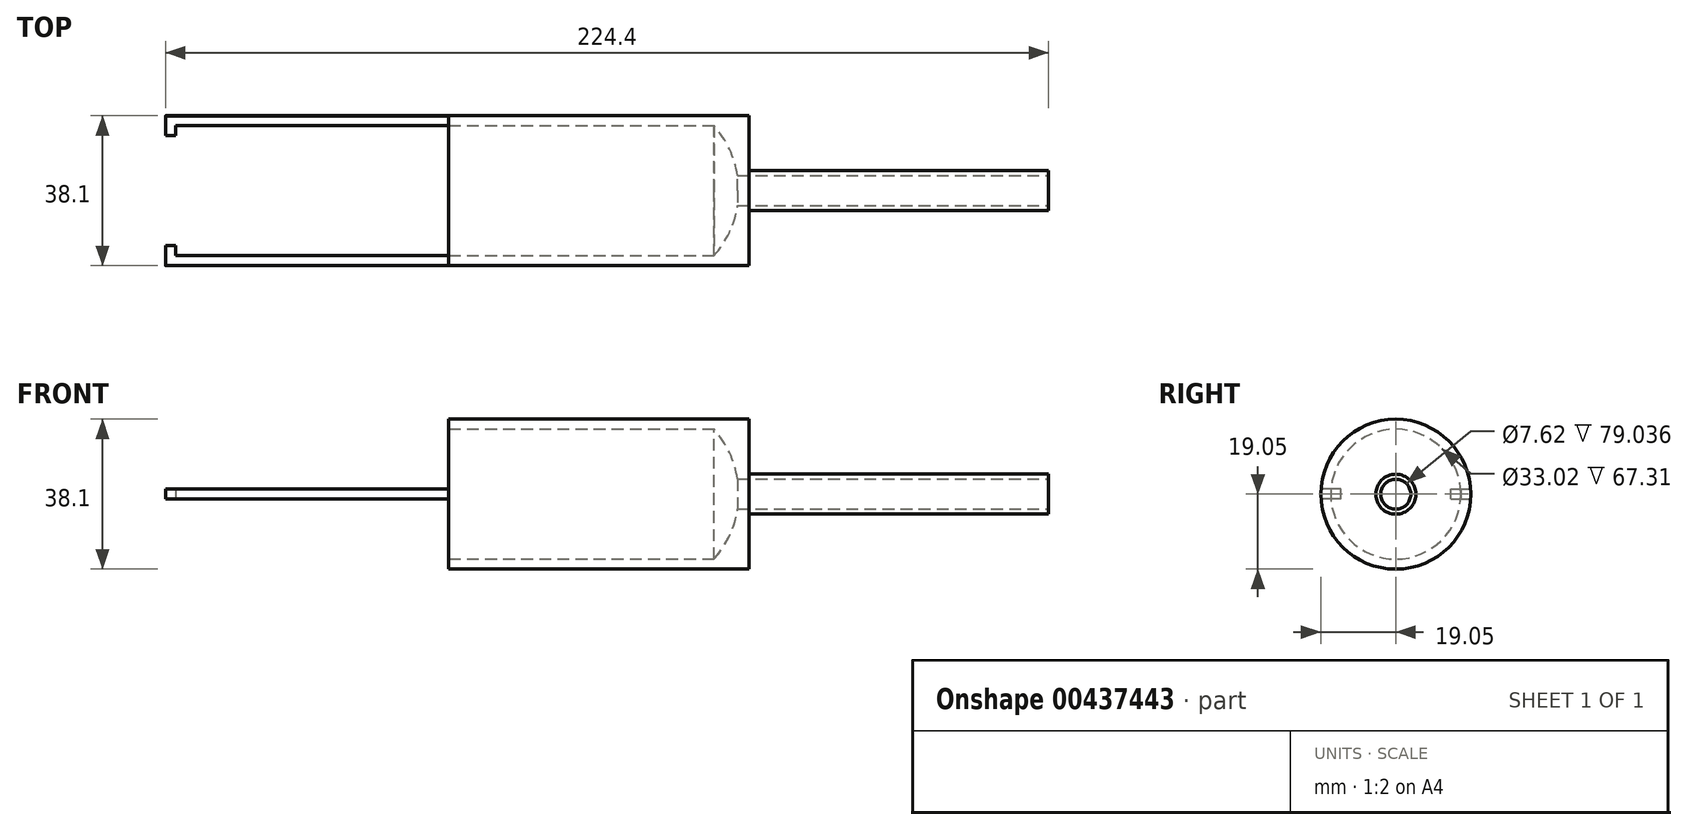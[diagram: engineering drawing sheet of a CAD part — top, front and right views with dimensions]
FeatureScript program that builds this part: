
annotation { "Feature Type Name" : "Feature", "Feature Type Description" : "" }
export const myFeature = defineFeature(function(context is Context, id is Id, definition is map)
    precondition{}
    {
        {
            var Q0;
            Q0=qCreatedBy(makeId("Right.planeOp"),FACE);
            var sketch = newSketch(context, id + "F0", { "sketchPlane" : qUnion([Q0])});
            skCircle(sketch, "E0", {"center": v(0, 0) * mm, "radius": 19.05 * mm});
            skSolve(sketch);
        }
        {
            var Q0;
            Q0=makeQuery(id+"F0.imprint","IMPRINT",FACE,{"disambiguationData":[TD([[makeQuery(id+"F0.imprint","IMPRINT",EDGE,{"derivedFrom":sQuery(id+"F0.wireOp",EDGE,"E0")}),1.0]])]});
            extrude(context, id + "F1", {"entities" : qUnion([Q0]), "depth" : -76.2 * mm});
        }
        {
            var Q0;
            Q0=makeQuery(id+"F1.opExtrude","CAP_FACE",FACE,{"disambiguationData":[OSD([sQuery(id+"F0.wireOp",EDGE,"E0")])],"isStart":true});
            var sketch = newSketch(context, id + "F2", { "sketchPlane" : qUnion([Q0])});
            skCircle(sketch, "E1", {"center": v(0, 0) * mm, "radius": 5.08 * mm});
            skSolve(sketch);
        }
        {
            var Q0;
            Q0=makeQuery(id+"F2.imprint","IMPRINT",FACE,{"disambiguationData":[TD([[makeQuery(id+"F2.imprint","IMPRINT",EDGE,{"derivedFrom":sQuery(id+"F2.wireOp",EDGE,"E1")}),1.0]])]});
            extrude(context, id + "F3", {"entities" : qUnion([Q0]), "operationType" : NewBodyOperationType.ADD, "depth" : 76.2 * mm});
        }
        {
            var Q0;
            Q0=makeQuery(id+"F3.opExtrude","CAP_FACE",FACE,{"disambiguationData":[OSD([sQuery(id+"F2.wireOp",EDGE,"E1")])],"isStart":false});
            var sketch = newSketch(context, id + "F4", { "sketchPlane" : qUnion([Q0])});
            skCircle(sketch, "E2", {"center": v(0, 0) * mm, "radius": 3.81 * mm});
            skSolve(sketch);
        }
        {
            var Q0;
            Q0=makeQuery(id+"F4.imprint","IMPRINT",FACE,{"disambiguationData":[TD([[makeQuery(id+"F4.imprint","IMPRINT",EDGE,{"derivedFrom":sQuery(id+"F4.wireOp",EDGE,"E2")}),1.0]])]});
            extrude(context, id + "F5", {"entities" : qUnion([Q0]), "operationType" : NewBodyOperationType.REMOVE, "oppositeDirection" : true, "depth" : 88.9 * mm});
        }
        {
            var Q0;
            Q0=qCreatedBy(makeId("Front.planeOp"),FACE);
            var sketch = newSketch(context, id + "F6", { "sketchPlane" : qUnion([Q0])});
            skLineSegment(sketch, "E3", {"start": v(-76.2, 0) * mm, "end": v(-2.54, 0) * mm});
            skPoint(sketch, "E4", {"position": v(-8.9, 0) * mm});
            skLineSegment(sketch, "E5", {"start": v(-8.9, -16.51) * mm, "end": v(-8.9, 0) * mm});
            skArc(sketch, "E6", {"start": v(-8.9, -16.51) * mm, "mid": v(-4.18, -8.84) * mm, "end": v(-2.54, 0) * mm});
            skPoint(sketch, "E7.orphan", {"position": v(-8.9, 16.51) * mm});
            skLineSegment(sketch, "E8", {"start": v(-76.2, 0) * mm, "end": v(-76.2, -16.51) * mm});
            skLineSegment(sketch, "E9", {"start": v(-76.2, -16.51) * mm, "end": v(-8.9, -16.51) * mm});
            skSolve(sketch);
        }
        {
            var Q0;
            Q0 = qSketchRegion(id + "F6", true);
            var Q1;
            Q1=sQuery(id+"F6.wireOp",EDGE,"E3");
            revolve(context, id + "F7", {"operationType" : NewBodyOperationType.REMOVE, "entities" : qUnion([Q0]), "axis" : qUnion([Q1]), "revolveType" : RevolveType.FULL, "oppositeDirection" : true});
        }
        {
            var Q0;
            Q0=makeQuery(id+"F1.opExtrude","CAP_FACE",FACE,{"disambiguationData":[OSD([sQuery(id+"F0.wireOp",EDGE,"E0")])],"isStart":false});
            var sketch = newSketch(context, id + "F8", { "sketchPlane" : qUnion([Q0])});
            skLineSegment(sketch, "E10", {"start": v(19.05, 0) * mm, "end": v(-19.05, 0) * mm});
            skPoint(sketch, "E11", {"position": v(-16.51, 0) * mm});
            skPoint(sketch, "E12", {"position": v(16.51, 0) * mm});
            skLineSegment(sketch, "E13", {"start": v(16.51, 0) * mm, "end": v(16.51, 1.27) * mm});
            skLineSegment(sketch, "E14", {"start": v(16.51, 0) * mm, "end": v(16.51, -1.27) * mm});
            skLineSegment(sketch, "E15", {"start": v(16.51, 1.27) * mm, "end": v(13.97, 1.27) * mm});
            skLineSegment(sketch, "E16", {"start": v(16.51, -1.27) * mm, "end": v(13.97, -1.27) * mm});
            skLineSegment(sketch, "E17", {"start": v(13.97, -1.27) * mm, "end": v(13.97, 1.27) * mm});
            skLineSegment(sketch, "E18", {"start": v(0, 0) * mm, "end": v(0, -5.83) * mm});
            skLineSegment(sketch, "E19.MirrorCS", {"start": v(-16.51, 1.27) * mm, "end": v(-13.97, 1.27) * mm});
            skLineSegment(sketch, "E20.MirrorCS", {"start": v(-13.97, -1.27) * mm, "end": v(-13.97, 1.27) * mm});
            skLineSegment(sketch, "E21.MirrorCS", {"start": v(-16.51, -1.27) * mm, "end": v(-13.97, -1.27) * mm});
            skLineSegment(sketch, "E22.MirrorCS", {"start": v(-16.51, 0) * mm, "end": v(-16.51, 1.27) * mm});
            skLineSegment(sketch, "E23.MirrorCS", {"start": v(-16.51, 0) * mm, "end": v(-16.51, -1.27) * mm});
            skLineSegment(sketch, "E24", {"start": v(-16.51, 1.27) * mm, "end": v(-19, 1.27) * mm});
            skLineSegment(sketch, "E25", {"start": v(-16.51, -1.27) * mm, "end": v(-19, -1.27) * mm});
            skLineSegment(sketch, "E26", {"start": v(16.51, -1.27) * mm, "end": v(19, -1.27) * mm});
            skLineSegment(sketch, "E27", {"start": v(16.51, 1.27) * mm, "end": v(19, 1.27) * mm});
            skSolve(sketch);
        }
        {
            var Q0;
            {var subQ3=sQuery(id+"F8.wireOp",EDGE,"E22.MirrorCS");Q0=makeQuery(id+"F8.imprint","IMPRINT",FACE,{"disambiguationData":[TD([[makeQuery(id+"F8.imprint","IMPRINT",EDGE,{"derivedFrom":subQ3}),1.0]])]});}
            var Q1;
            {var subQ3=sQuery(id+"F8.wireOp",EDGE,"E23.MirrorCS");Q1=makeQuery(id+"F8.imprint","IMPRINT",FACE,{"disambiguationData":[TD([[makeQuery(id+"F8.imprint","IMPRINT",EDGE,{"derivedFrom":subQ3}),-1.0]])]});}
            var Q2;
            {var subQ3=sQuery(id+"F8.wireOp",EDGE,"E13");Q2=makeQuery(id+"F8.imprint","IMPRINT",FACE,{"disambiguationData":[TD([[makeQuery(id+"F8.imprint","IMPRINT",EDGE,{"derivedFrom":subQ3}),-1.0]])]});}
            var Q3;
            {var subQ3=sQuery(id+"F8.wireOp",EDGE,"E14");Q3=makeQuery(id+"F8.imprint","IMPRINT",FACE,{"disambiguationData":[TD([[makeQuery(id+"F8.imprint","IMPRINT",EDGE,{"derivedFrom":subQ3}),1.0]])]});}
            extrude(context, id + "F9", {"entities" : qUnion([Q0, Q1, Q2, Q3]), "depth" : 72 * mm});
        }
        {
            var Q0;
            Q0=makeQuery(id+"F9.opExtrude","SWEPT_FACE",FACE,{"disambiguationData":[OSD([sQuery(id+"F8.wireOp",EDGE,"E13"),sQuery(id+"F8.wireOp",EDGE,"E14")])]});
            var sketch = newSketch(context, id + "F10", { "sketchPlane" : qUnion([Q0])});
            skLineSegment(sketch, "E28.bottom", {"start": v(148.2, 1.27) * mm, "end": v(145.66, 1.27) * mm});
            skLineSegment(sketch, "E28.top", {"start": v(148.2, -1.27) * mm, "end": v(145.66, -1.27) * mm});
            skLineSegment(sketch, "E28.left", {"start": v(148.2, 1.27) * mm, "end": v(148.2, -1.27) * mm});
            skLineSegment(sketch, "E28.right", {"start": v(145.66, 1.27) * mm, "end": v(145.66, -1.27) * mm});
            skSolve(sketch);
        }
        {
            var Q0;
            Q0=makeQuery(id+"F10.imprint","IMPRINT",FACE,{"disambiguationData":[TD([[makeQuery(id+"F10.imprint","IMPRINT",EDGE,{"derivedFrom":sQuery(id+"F10.wireOp",EDGE,"E28.bottom")}),1.0]])]});
            extrude(context, id + "F11", {"entities" : qUnion([Q0]), "operationType" : NewBodyOperationType.ADD, "depth" : 2.54 * mm});
        }
        {
            var Q0;
            Q0=makeQuery(id+"F9.opExtrude","SWEPT_FACE",FACE,{"disambiguationData":[OSD([sQuery(id+"F8.wireOp",EDGE,"E22.MirrorCS"),sQuery(id+"F8.wireOp",EDGE,"E23.MirrorCS")])]});
            var sketch = newSketch(context, id + "F12", { "sketchPlane" : qUnion([Q0])});
            skLineSegment(sketch, "E29.bottom", {"start": v(-148.2, 1.27) * mm, "end": v(-145.66, 1.27) * mm});
            skLineSegment(sketch, "E29.top", {"start": v(-148.2, -1.27) * mm, "end": v(-145.66, -1.27) * mm});
            skLineSegment(sketch, "E29.left", {"start": v(-148.2, 1.27) * mm, "end": v(-148.2, -1.27) * mm});
            skLineSegment(sketch, "E29.right", {"start": v(-145.66, 1.27) * mm, "end": v(-145.66, -1.27) * mm});
            skSolve(sketch);
        }
        {
            var Q0;
            Q0=makeQuery(id+"F12.imprint","IMPRINT",FACE,{"disambiguationData":[TD([[makeQuery(id+"F12.imprint","IMPRINT",EDGE,{"derivedFrom":sQuery(id+"F12.wireOp",EDGE,"E29.bottom")}),-1.0]])]});
            extrude(context, id + "F13", {"entities" : qUnion([Q0]), "operationType" : NewBodyOperationType.ADD, "depth" : 2.54 * mm});
        }
    });
